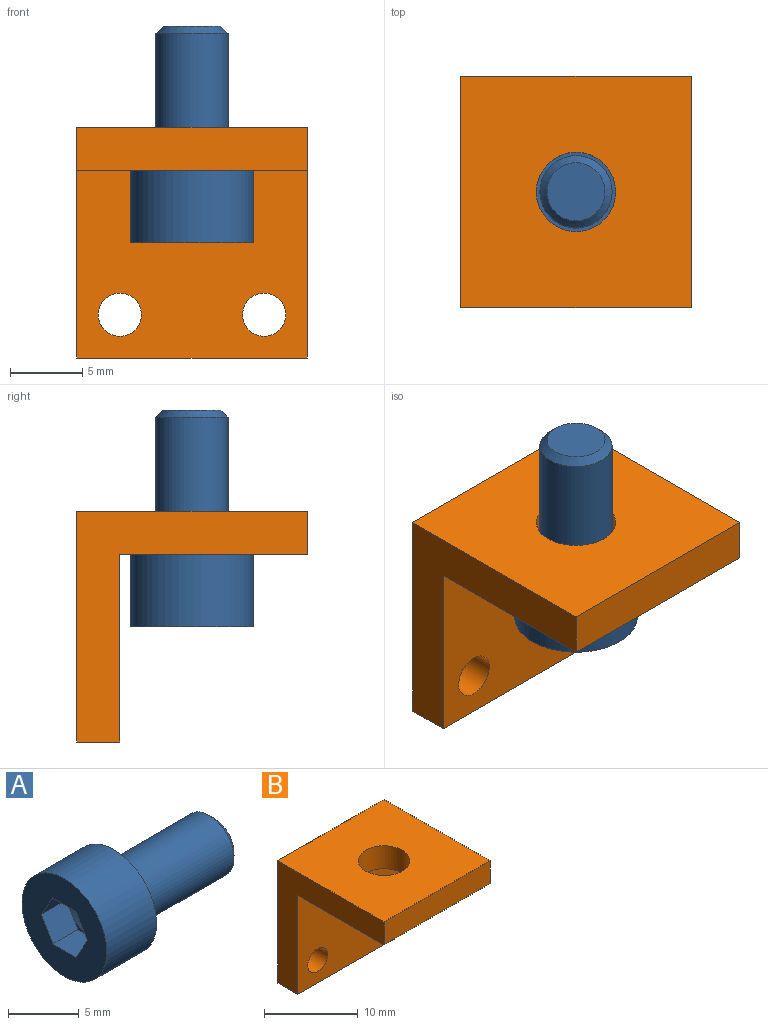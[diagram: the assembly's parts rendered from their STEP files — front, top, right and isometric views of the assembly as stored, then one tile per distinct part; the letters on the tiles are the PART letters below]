
ASSEMBLY  parts=2 mates=1
PART A: 14 faces, bbox 15x8.5x8.5 mm
  f0: cylinder r=4.25mm len=8.5mm, axis (-1,0,0), area 133.5mm2, adj f12,f13
  f1: cylinder r=2.5mm len=9.51mm, axis (-1,0,0), area 149.4mm2, adj f2,f12
  f2: cone r=2.25mm half-angle=45deg, axis (-1,0,0), area 9.8mm2, adj f1,f11
  f3: cone r=0.99mm half-angle=60deg, axis (-1,0,0), area 14.4mm2, adj f10
  f4: plane 2.5x2mm, normal (0,-0.87,-0.5), area 5.8mm2, adj f5,f9,f10,f13
  f5: plane 2.5x2mm, normal (0,-0.87,0.5), area 5.8mm2, adj f4,f6,f10,f13
  f6: plane 2.5x2.31mm, normal (0,0,1), area 5.8mm2, adj f5,f7,f10,f13
  f7: plane 2.5x2mm, normal (0,0.87,0.5), area 5.8mm2, adj f6,f8,f10,f13
  f8: plane 2.5x2mm, normal (0,0.87,-0.5), area 5.8mm2, adj f7,f9,f10,f13
  f9: plane 2.5x2.31mm, normal (0,0,-1), area 5.8mm2, adj f4,f8,f10,f13
  f10: plane 4.62x4mm, normal (-1,0,0), area 1.4mm2, adj f3,f4,f5,f6,f7,f8,f9
  f11: plane 4.02x4.02mm, normal (1,0,0), area 12.7mm2, adj f2
  f12: plane 8.5x8.5mm, normal (1,0,0), area 37.1mm2, adj f0,f1
  f13: plane 8.5x8.5mm, normal (-1,0,0), area 42.9mm2, adj f0,f4,f5,f6,f7,f8,f9
PART B: 11 faces, bbox 16x16x16 mm
  f0: plane 16x16mm, normal (0,0,1), area 232.2mm2, adj f1,f5,f6,f7,f10
  f1: plane 16x3mm, normal (0,-1,0), area 48mm2, adj f0,f2,f6,f7
  f2: plane 16x13mm, normal (0,0,-1), area 184.2mm2, adj f1,f3,f6,f7,f10
  f3: plane 16x13mm, normal (0,-1,0), area 193.9mm2, adj f2,f4,f6,f7,f8,f9
  f4: plane 16x3mm, normal (0,0,-1), area 48mm2, adj f3,f5,f6,f7
  f5: plane 16x16mm, normal (0,1,0), area 241.9mm2, adj f0,f4,f6,f7,f8,f9
  f6: plane 16x16mm, normal (1,0,0), area 87mm2, adj f0,f1,f2,f3,f4,f5
  f7: plane 16x16mm, normal (-1,0,0), area 87mm2, adj f0,f1,f2,f3,f4,f5
  f8: cylinder r=1.5mm len=3mm, axis (0,-1,0), area 28.3mm2, adj f3,f5
  f9: cylinder r=1.5mm len=3mm, axis (0,-1,0), area 28.3mm2, adj f3,f5
  f10: cylinder r=2.75mm len=5.5mm, axis (0,0,1), area 51.8mm2, adj f0,f2
PLACE A rot(axis=(0,-1,0),90deg) t=(-16.88,-9.46,5.43)mm
PLACE B t=(-24.88,29.77,-36.67)mm
MATE fastened A.f0 <-> B.f10  axis (0,0,1) through (-16.88,-9.46,5.43)mm
